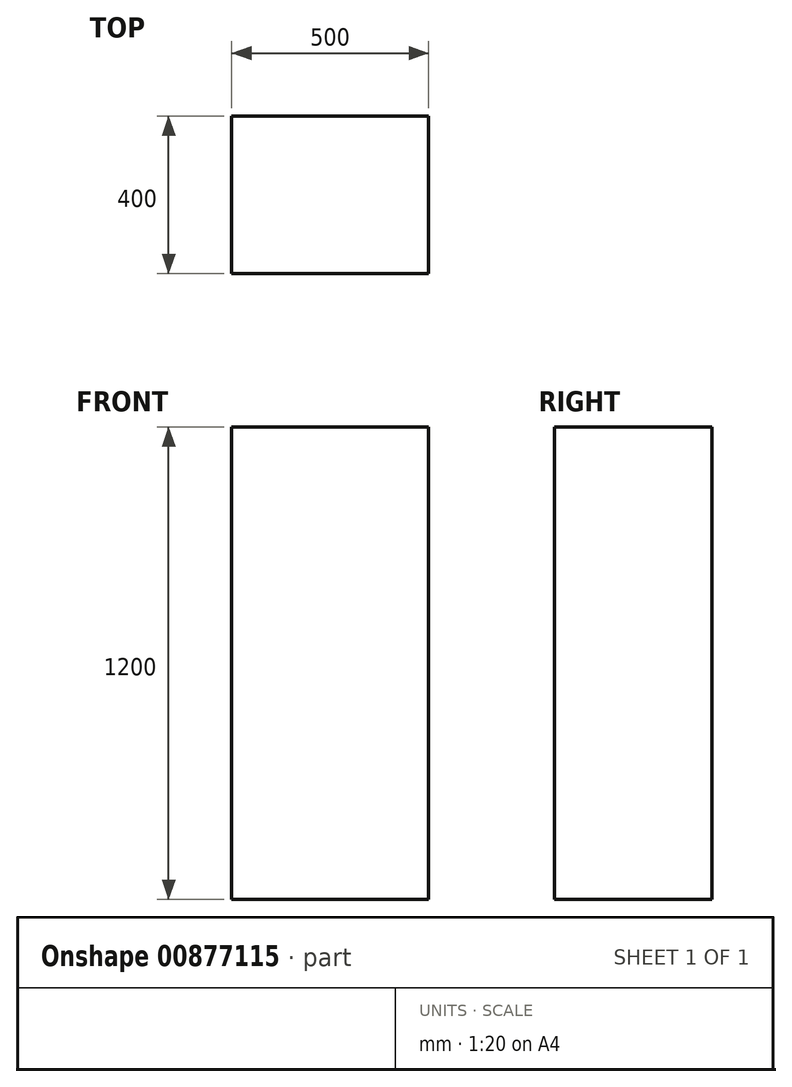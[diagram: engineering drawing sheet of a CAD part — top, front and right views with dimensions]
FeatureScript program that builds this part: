
annotation { "Feature Type Name" : "Feature", "Feature Type Description" : "" }
export const myFeature = defineFeature(function(context is Context, id is Id, definition is map)
    precondition{}
    {
        {
            var Q0;
            Q0=qCreatedBy(makeId("Front.planeOp"),FACE);
            var sketch = newSketch(context, id + "F0", { "sketchPlane" : qUnion([Q0])});
            skLineSegment(sketch, "E0.bottom", {"start": v(250, 600) * mm, "end": v(-250, 600) * mm});
            skLineSegment(sketch, "E0.top", {"start": v(250, -600) * mm, "end": v(-250, -600) * mm});
            skLineSegment(sketch, "E0.left", {"start": v(250, 600) * mm, "end": v(250, -600) * mm});
            skLineSegment(sketch, "E0.right", {"start": v(-250, 600) * mm, "end": v(-250, -600) * mm});
            skPoint(sketch, "E0.middle", {"position": v(0, 0) * mm});
            skSolve(sketch);
        }
        {
            var Q0;
            Q0=makeQuery(id+"F0.imprint","IMPRINT",FACE,{"disambiguationData":[TD([[makeQuery(id+"F0.imprint","IMPRINT",EDGE,{"derivedFrom":sQuery(id+"F0.wireOp",EDGE,"E0.bottom")}),1.0]])]});
            extrude(context, id + "F1", {"entities" : qUnion([Q0]), "depth" : 400 * mm, "offsetDistance" : 25 * mm});
        }
    });
